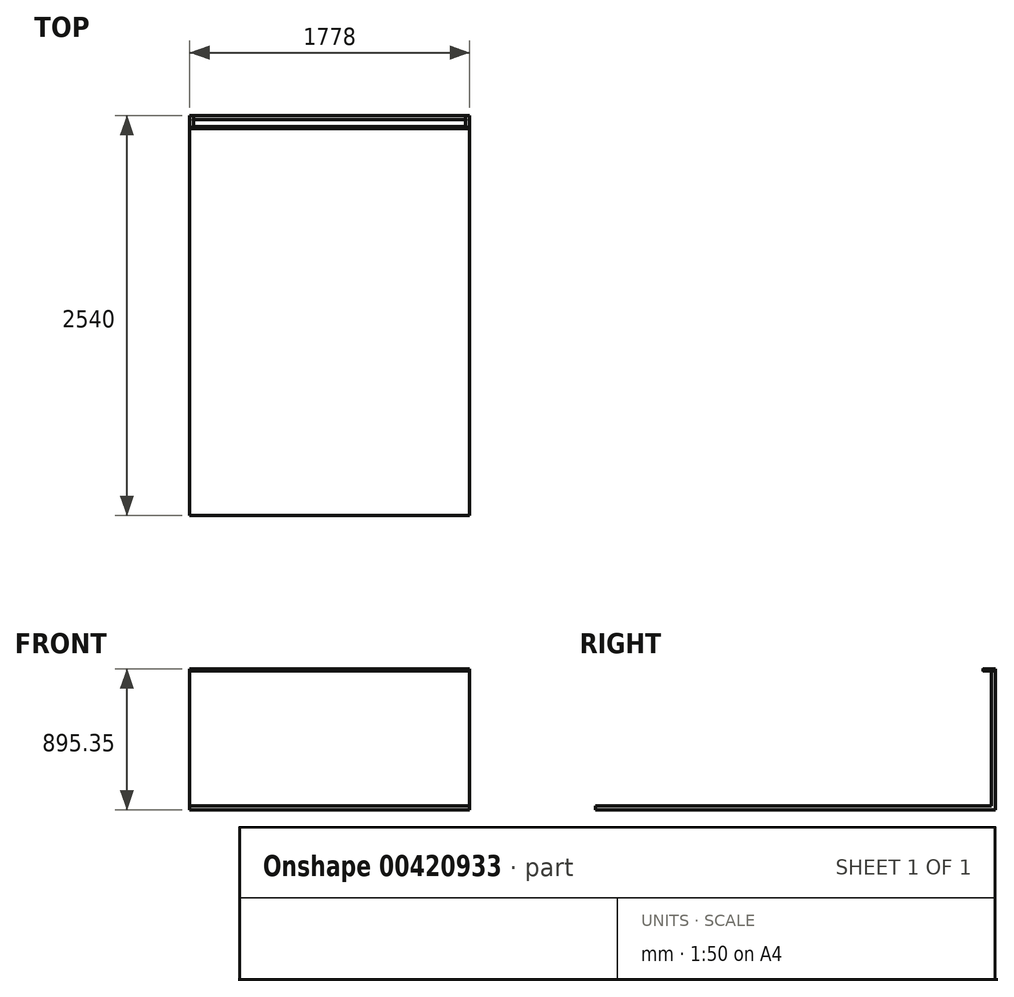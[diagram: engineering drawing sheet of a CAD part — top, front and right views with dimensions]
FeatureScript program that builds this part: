
annotation { "Feature Type Name" : "Feature", "Feature Type Description" : "" }
export const myFeature = defineFeature(function(context is Context, id is Id, definition is map)
    precondition{}
    {
        {
            var Q0;
            Q0=qCreatedBy(makeId("Top.planeOp"),FACE);
            var sketch = newSketch(context, id + "F0", { "sketchPlane" : qUnion([Q0])});
            skLineSegment(sketch, "E0.bottom", {"start": v(0, 0) * mm, "end": v(1778, 0) * mm});
            skLineSegment(sketch, "E0.top", {"start": v(0, -2540) * mm, "end": v(1778, -2540) * mm});
            skLineSegment(sketch, "E0.left", {"start": v(0, 0) * mm, "end": v(0, -2540) * mm});
            skLineSegment(sketch, "E0.right", {"start": v(1778, 0) * mm, "end": v(1778, -2540) * mm});
            skSolve(sketch);
        }
        {
            var Q0;
            Q0 = qSketchRegion(id + "F0", true);
            extrude(context, id + "F1", {"entities" : qUnion([Q0]), "oppositeDirection" : true, "depth" : 25.4 * mm});
        }
        {
            var Q0;
            Q0=qCreatedBy(makeId("Front.planeOp"),FACE);
            var sketch = newSketch(context, id + "F2", { "sketchPlane" : qUnion([Q0])});
            skLineSegment(sketch, "E1.bottom", {"start": v(0, 0) * mm, "end": v(1778, 0) * mm});
            skLineSegment(sketch, "E1.top", {"start": v(0, 863.6) * mm, "end": v(1778, 863.6) * mm});
            skLineSegment(sketch, "E1.left", {"start": v(0, 0) * mm, "end": v(0, 863.6) * mm});
            skLineSegment(sketch, "E1.right", {"start": v(1778, 0) * mm, "end": v(1778, 863.6) * mm});
            skSolve(sketch);
        }
        {
            var Q0;
            Q0 = qSketchRegion(id + "F2", true);
            extrude(context, id + "F3", {"entities" : qUnion([Q0]), "operationType" : NewBodyOperationType.ADD, "depth" : 25.4 * mm});
        }
        {
            var Q0;
            Q0=qCreatedBy(makeId("Right.planeOp"),FACE);
            var sketch = newSketch(context, id + "F4", { "sketchPlane" : qUnion([Q0])});
            skCircle(sketch, "E2", {"center": v(-76.2, 863.6) * mm, "radius": 6.35 * mm});
            skSolve(sketch);
        }
        {
            var Q0;
            Q0 = qSketchRegion(id + "F4", true);
            var Q1;
            Q1=makeQuery(id+"F3.boolean.opBoolean","MERGE",FACE,{"derivedFrom":[makeQuery(id+"F1.opExtrude","SWEPT_FACE",FACE,{"disambiguationData":[OSD([sQuery(id+"F0.wireOp",EDGE,"E0.right")])]}),makeQuery(id+"F3.opExtrude","SWEPT_FACE",FACE,{"disambiguationData":[OSD([sQuery(id+"F2.wireOp",EDGE,"E1.right")])]})]});
            extrude(context, id + "F5", {"entities" : qUnion([Q0]), "endBound" : BoundingType.UP_TO_SURFACE, "endBoundEntityFace" : qUnion([Q1]), "depth" : 25.4 * mm});
        }
        {
            var Q0;
            Q0=qCreatedBy(makeId("Right.planeOp"),FACE);
            var sketch = newSketch(context, id + "F6", { "sketchPlane" : qUnion([Q0])});
            skLineSegment(sketch, "E3.bottom", {"start": v(-76.2, 869.95) * mm, "end": v(0, 869.95) * mm});
            skLineSegment(sketch, "E3.top", {"start": v(-76.2, 857.25) * mm, "end": v(0, 857.25) * mm});
            skLineSegment(sketch, "E3.left", {"start": v(-76.2, 869.95) * mm, "end": v(-76.2, 857.25) * mm});
            skLineSegment(sketch, "E3.right", {"start": v(0, 869.95) * mm, "end": v(0, 857.25) * mm});
            skSolve(sketch);
        }
        {
            var Q0;
            Q0 = qSketchRegion(id + "F6", true);
            extrude(context, id + "F7", {"entities" : qUnion([Q0]), "depth" : 25.4 * mm});
        }
        {
            var Q0;
            Q0=makeQuery(id+"F3.boolean.opBoolean","MERGE",FACE,{"derivedFrom":[makeQuery(id+"F1.opExtrude","SWEPT_FACE",FACE,{"disambiguationData":[OSD([sQuery(id+"F0.wireOp",EDGE,"E0.right")])]}),makeQuery(id+"F3.opExtrude","SWEPT_FACE",FACE,{"disambiguationData":[OSD([sQuery(id+"F2.wireOp",EDGE,"E1.right")])]})]});
            cPlane(context, id + "F8", {"entities" : qUnion([Q0]), "cplaneType" : CPlaneType.OFFSET, "offset" : 0 * mm, "width" : 152.4 * mm, "height" : 152.4 * mm});
        }
        {
            var Q0;
            Q0=qCreatedBy(id+"F8.planeOp",FACE);
            var sketch = newSketch(context, id + "F9", { "sketchPlane" : qUnion([Q0])});
            skLineSegment(sketch, "E4.0", {"start": v(-76.2, 869.95) * mm, "end": v(0, 869.95) * mm});
            skLineSegment(sketch, "E4.1", {"start": v(-76.2, 857.25) * mm, "end": v(0, 857.25) * mm});
            skLineSegment(sketch, "E4.2", {"start": v(-76.2, 869.95) * mm, "end": v(-76.2, 857.25) * mm});
            skLineSegment(sketch, "E4.3", {"start": v(0, 869.95) * mm, "end": v(0, 857.25) * mm});
            skSolve(sketch);
        }
        {
            var Q0;
            Q0 = qSketchRegion(id + "F9", true);
            extrude(context, id + "F10", {"entities" : qUnion([Q0]), "oppositeDirection" : true, "depth" : 25.4 * mm});
        }
    });
